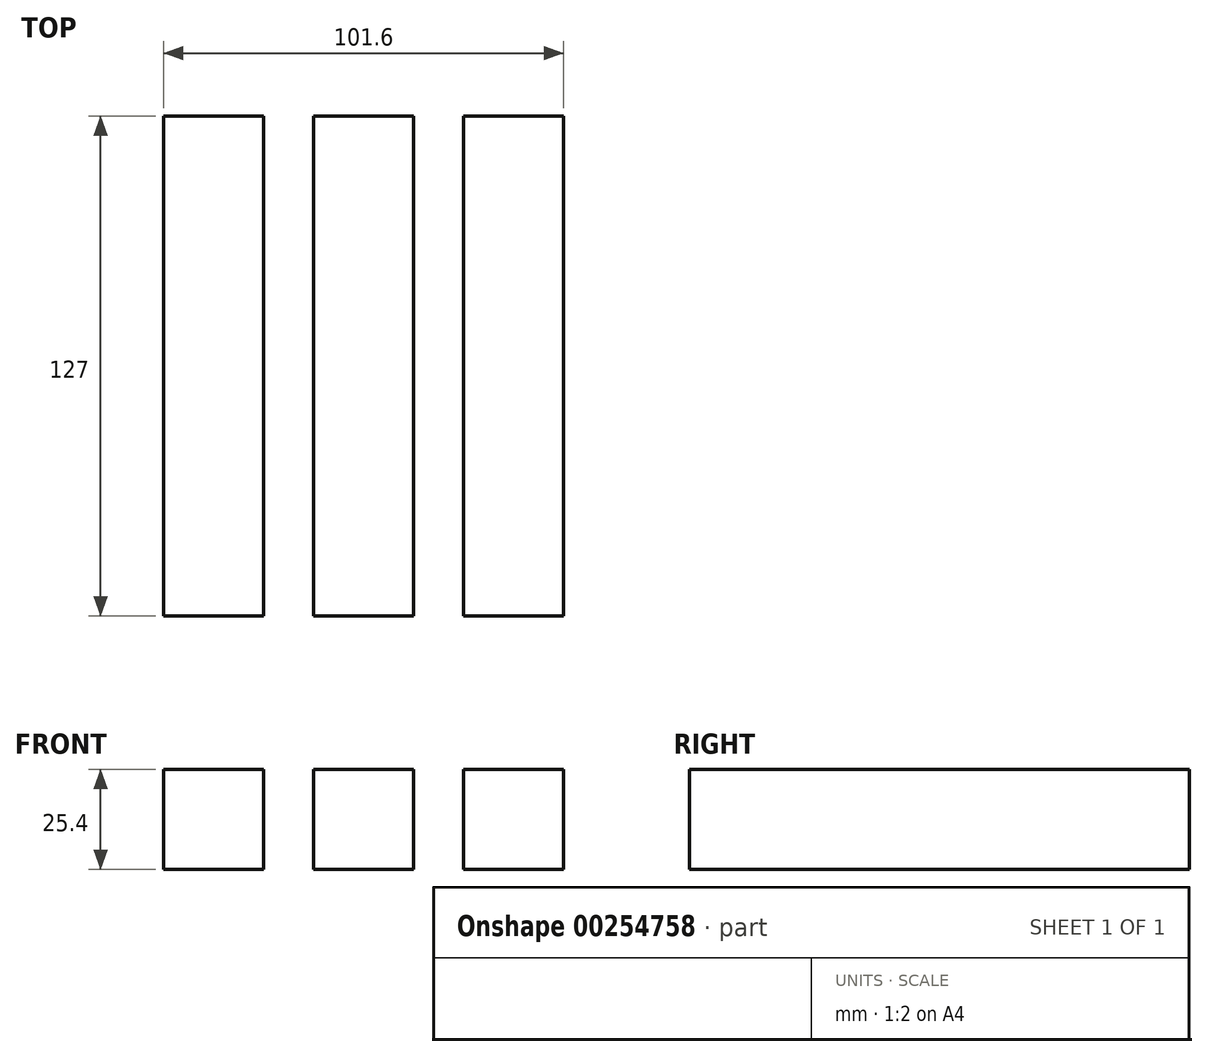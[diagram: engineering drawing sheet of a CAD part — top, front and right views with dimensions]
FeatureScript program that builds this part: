
annotation { "Feature Type Name" : "Feature", "Feature Type Description" : "" }
export const myFeature = defineFeature(function(context is Context, id is Id, definition is map)
    precondition{}
    {
        {
            var Q0;
            Q0=qCreatedBy(makeId("Front.planeOp"),FACE);
            var sketch = newSketch(context, id + "F0", { "sketchPlane" : qUnion([Q0])});
            skLineSegment(sketch, "E0.bottom", {"start": v(-12.7, 12.7) * mm, "end": v(12.7, 12.7) * mm});
            skLineSegment(sketch, "E0.top", {"start": v(-12.7, -12.7) * mm, "end": v(12.7, -12.7) * mm});
            skLineSegment(sketch, "E0.left", {"start": v(-12.7, 12.7) * mm, "end": v(-12.7, -12.7) * mm});
            skLineSegment(sketch, "E0.right", {"start": v(12.7, 12.7) * mm, "end": v(12.7, -12.7) * mm});
            skPoint(sketch, "E0.middle", {"position": v(0, 0) * mm});
            skLineSegment(sketch, "E1", {"start": v(0, 0) * mm, "end": v(38.1, 0) * mm});
            skPoint(sketch, "E1.endSnap0", {"position": v(12.7, 0) * mm});
            skLineSegment(sketch, "E2.bottom", {"start": v(25.4, 12.7) * mm, "end": v(50.8, 12.7) * mm});
            skLineSegment(sketch, "E2.top", {"start": v(25.4, -12.7) * mm, "end": v(50.8, -12.7) * mm});
            skLineSegment(sketch, "E2.left", {"start": v(25.4, 12.7) * mm, "end": v(25.4, -12.7) * mm});
            skLineSegment(sketch, "E2.right", {"start": v(50.8, 12.7) * mm, "end": v(50.8, -12.7) * mm});
            skPoint(sketch, "E2.middle", {"position": v(38.1, 0) * mm});
            skLineSegment(sketch, "E3", {"start": v(0, 0) * mm, "end": v(-38.1, 0) * mm});
            skLineSegment(sketch, "E4.bottom", {"start": v(-50.8, 12.7) * mm, "end": v(-25.4, 12.7) * mm});
            skLineSegment(sketch, "E4.top", {"start": v(-50.8, -12.7) * mm, "end": v(-25.4, -12.7) * mm});
            skLineSegment(sketch, "E4.left", {"start": v(-50.8, 12.7) * mm, "end": v(-50.8, -12.7) * mm});
            skLineSegment(sketch, "E4.right", {"start": v(-25.4, 12.7) * mm, "end": v(-25.4, -12.7) * mm});
            skPoint(sketch, "E4.middle", {"position": v(-38.1, 0) * mm});
            skSolve(sketch);
        }
        {
            var Q0;
            Q0 = qSketchRegion(id + "F0", true);
            extrude(context, id + "F1", {"entities" : qUnion([Q0]), "endBound" : BoundingType.SYMMETRIC, "depth" : 127 * mm});
        }
    });
